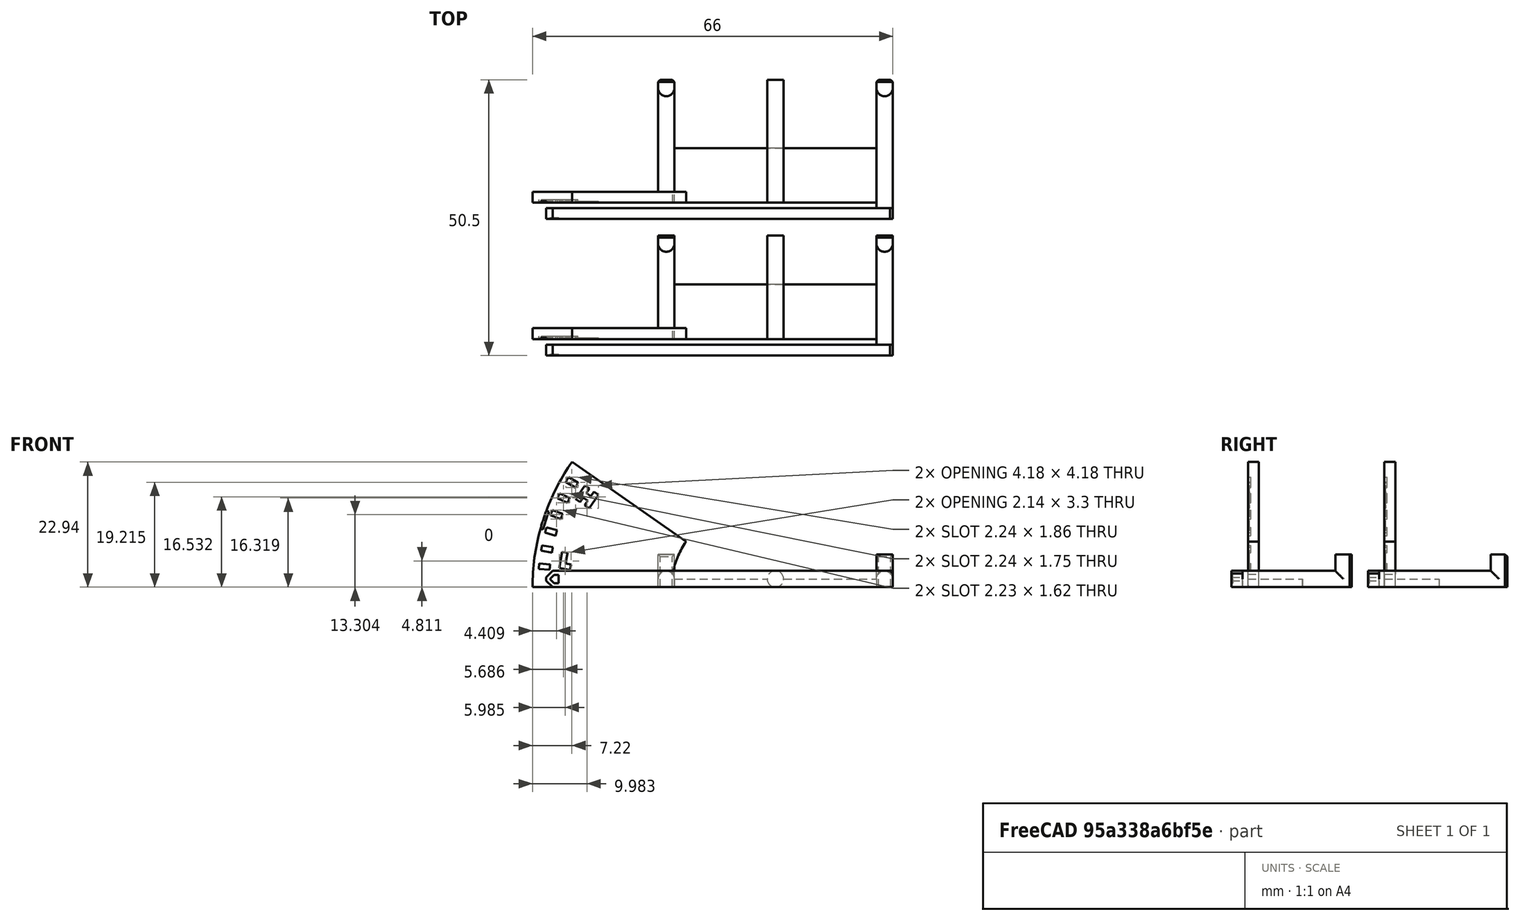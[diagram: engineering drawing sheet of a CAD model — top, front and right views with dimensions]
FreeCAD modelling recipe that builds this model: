
FCSTD DOCUMENT  (FreeCAD 0.18R16146 (Git))
Label: belt-tension-meter-lite
License: All rights reserved
LicenseURL: http://en.wikipedia.org/wiki/All_rights_reserved
objects: Part::Box×20, Part::Cylinder×11, Part::Cut×8, Part::MultiFuse×6, Part::Chamfer×4, Part::Feature×4, Part::MultiCommon×2, Mesh::Feature×1
note: 55 computed .brp shape members not serialized (recipe doc carries the construction recipe); baked Part::Feature solids carry a one-line shape summary decoded from their .brp

FEATURE [Mesh::Feature] belt
  Placement = pos=(-127.5,-93.9,0) rot=(0,0,1;0rad)
FEATURE [Part::Cylinder] Cylinder
  Angle = 35
  AttacherType = Attacher::AttachEngine3D
  Height = 2
  Placement = pos=(17,3,-1e-15) rot=(0,0.707107,0.707107;3.14159rad)
  Radius = 40
FEATURE [Part::Cylinder] Cylinder001
  Angle = 360
  AttacherType = Attacher::AttachEngine3D
  Height = 2
  Placement = pos=(17,3,-1e-15) rot=(-1,0,0;1.5708rad)
  Radius = 14.5
FEATURE [Part::Box] Box  label="Cube"
  AttacherType = Attacher::AttachEngine3D
  Height = 3
  Length = 63.5
  Placement = pos=(-20.5,0,0) rot=(0,0,1;0rad)
  Width = 2
FEATURE [Part::Cylinder] Cylinder002
  Angle = 360
  AttacherType = Attacher::AttachEngine3D
  Height = 19
  Placement = pos=(1.5,3,1.5) rot=(-1,0,0;1.5708rad)
  Radius = 1.5
FEATURE [Part::Cylinder] Cylinder003
  Angle = 360
  AttacherType = Attacher::AttachEngine3D
  Height = 4.5
  Placement = pos=(1.5,20.5,1.5) rot=(0,0,1;0rad)
  Radius = 1.5
FEATURE [Part::Cylinder] Cylinder004
  Angle = 360
  AttacherType = Attacher::AttachEngine3D
  Height = 19
  Placement = pos=(21.5,3,1.5) rot=(-1,0,0;1.5708rad)
  Radius = 1.5
FEATURE [Part::Cylinder] Cylinder005
  Angle = 360
  AttacherType = Attacher::AttachEngine3D
  Height = 22
  Placement = pos=(41.5,0,1.5) rot=(-1,0,0;1.5708rad)
  Radius = 1.5
FEATURE [Part::Cylinder] Cylinder006
  Angle = 360
  AttacherType = Attacher::AttachEngine3D
  Height = 4.5
  Placement = pos=(41.5,20.5,1.5) rot=(0,0,1;0rad)
  Radius = 1.5
FEATURE [Part::Box] Box001  label="Cube001"
  AttacherType = Attacher::AttachEngine3D
  Height = 1.5
  Length = 43
  Placement = pos=(0,3,0) rot=(0,0,1;0rad)
  Width = 10
FEATURE [Part::Box] Box002  label="Cube002"
  AttacherType = Attacher::AttachEngine3D
  Height = 1.5
  Length = 3
  Placement = pos=(40,2,0) rot=(0,0,1;0rad)
  Width = 20
FEATURE [Part::Box] Box003  label="Cube003"
  AttacherType = Attacher::AttachEngine3D
  Height = 1.5
  Length = 3
  Placement = pos=(0,3,0) rot=(0,0,1;0rad)
  Width = 19
FEATURE [Part::Box] Box004  label="Cube004"
  AttacherType = Attacher::AttachEngine3D
  Height = 6
  Length = 3
  Placement = pos=(0,20.5,0) rot=(0,0,1;0rad)
  Width = 1.5
FEATURE [Part::Box] Box005  label="Cube005"
  AttacherType = Attacher::AttachEngine3D
  Height = 6
  Length = 3
  Placement = pos=(40,20.5,0) rot=(0,0,1;0rad)
  Width = 1.5
FEATURE [Part::Cylinder] Cylinder007
  Angle = 360
  AttacherType = Attacher::AttachEngine3D
  Height = 15
  Placement = pos=(17,3,-1e-15) rot=(-1,0,0;1.5708rad)
  Radius = 37
FEATURE [Part::Box] Box007  label="Cube007"
  AttacherType = Attacher::AttachEngine3D
  Height = 63
  Length = 1
  Placement = pos=(16.5,3,0) rot=(0,-1,0;1.48353rad)
  Width = 0.5
FEATURE [Part::Box] Box008  label="Cube008"
  AttacherType = Attacher::AttachEngine3D
  Height = 63
  Length = 1
  Placement = pos=(16.5,3,0) rot=(0,-1,0;1.39626rad)
  Width = 0.5
FEATURE [Part::Box] Box009  label="Cube009"
  AttacherType = Attacher::AttachEngine3D
  Height = 63
  Length = 1
  Placement = pos=(16.5,3,0) rot=(0,-1,0;1.309rad)
  Width = 0.5
FEATURE [Part::Box] Box010  label="Cube010"
  AttacherType = Attacher::AttachEngine3D
  Height = 63
  Length = 1
  Placement = pos=(16.5,3,0) rot=(0,-1,0;1.22173rad)
  Width = 0.5
FEATURE [Part::Box] Box011  label="Cube011"
  AttacherType = Attacher::AttachEngine3D
  Height = 63
  Length = 1
  Placement = pos=(16.5,3,0) rot=(0,-1,0;1.13446rad)
  Width = 0.5
FEATURE [Part::Box] Box012  label="Cube012"
  AttacherType = Attacher::AttachEngine3D
  Height = 63
  Length = 1
  Placement = pos=(16.5,3,0) rot=(0,-1,0;1.0472rad)
  Width = 0.5
FEATURE [Part::MultiFuse] Fusion
  Shapes = -> [Box012,Box011,Box010,Box009,Box008,Box007]
FEATURE [Part::Cut] Cut
  Base = -> Cylinder
  Tool = -> Cylinder001
FEATURE [Part::Cylinder] Cylinder008
  Angle = 360
  AttacherType = Attacher::AttachEngine3D
  Height = 15
  Placement = pos=(17,3,-1e-15) rot=(-1,0,0;1.5708rad)
  Radius = 39
FEATURE [Part::MultiCommon] Common
  Shapes = -> [Fusion,Cylinder008]
FEATURE [Part::Cut] Cut001
  Base = -> Common
  Tool = -> Cylinder007
FEATURE [Part::Cut] Cut002
  Base = -> Cut
  Tool = -> Cut001
FEATURE [Part::Chamfer] Chamfer
  Base = -> Box
  Edges = 2 edges r=1.2: [Edge2,Edge4]
FEATURE [Part::MultiFuse] Fusion001
  Shapes = -> [Chamfer,Box001,Box002,Cut002,Cylinder003,Box003,Cylinder004,Box004,Cylinder005,Box005,Cylinder006,Cylinder002]
FEATURE [Part::Box] Box013  label="Cube013"
  AttacherType = Attacher::AttachEngine3D
  Height = 3
  Length = 1
  Width = 1
FEATURE [Part::Box] Box014  label="Cube014"
  AttacherType = Attacher::AttachEngine3D
  Height = 3
  Length = 1
  Placement = pos=(2,0,0) rot=(0,0,1;0rad)
  Width = 1
FEATURE [Part::Box] Box015  label="Cube015"
  AttacherType = Attacher::AttachEngine3D
  Height = 1
  Length = 1
  Placement = pos=(1,0,1) rot=(0,0,1;0rad)
  Width = 1
FEATURE [Part::MultiFuse] Fusion002
  Placement = pos=(-15.1059,0,16.164) rot=(0,1,0;0.610865rad)
  Shapes = -> [Box015,Box014,Box013]
FEATURE [Part::Box] Box016  label="Cube016"
  AttacherType = Attacher::AttachEngine3D
  Height = 3
  Length = 1
  Width = 1
FEATURE [Part::Box] Box017  label="Cube017"
  AttacherType = Attacher::AttachEngine3D
  Height = 1
  Length = 1
  Placement = pos=(1,0,0) rot=(0,0,1;0rad)
  Width = 1
FEATURE [Part::MultiFuse] Fusion003
  Placement = pos=(-18.0868,0,3.5076) rot=(0,1,0;0.174533rad)
  Shapes = -> [Box017,Box016]
FEATURE [Part::MultiFuse] Fusion004
  Placement = pos=(0,2.25,0) rot=(0,0,1;0rad)
  Shapes = -> [Fusion002,Fusion003]
FEATURE [Part::Cut] Cut003
  Base = -> Fusion001
  Tool = -> Fusion004
FEATURE [Part::Cylinder] Cylinder009
  Angle = 5
  AttacherType = Attacher::AttachEngine3D
  Height = 15
  Placement = pos=(17,3,-1e-15) rot=(0.09579,0.703855,0.703855;3.33259rad)
  Radius = 39.5
FEATURE [Part::Cylinder] Cylinder010
  Angle = 5
  AttacherType = Attacher::AttachEngine3D
  Height = 15
  Placement = pos=(17,3,-1e-15) rot=(0.09579,0.703855,0.703855;3.33259rad)
  Radius = 40
FEATURE [Part::Cut] Cut004
  Base = -> Cylinder010
  Placement = pos=(0,-14.75,0) rot=(0,0,1;0rad)
  Tool = -> Cylinder009
FEATURE [Part::Cut] Cut005
  Base = -> Cut003
  Tool = -> Cut004
FEATURE [Part::Box] Box018  label="Cube018"
  AttacherType = Attacher::AttachEngine3D
  Height = 1.5
  Length = 1.5
  Placement = pos=(-19.75,-1,0.75) rot=(0,0,1;0rad)
  Width = 1
FEATURE [Part::Chamfer] Chamfer001
  Base = -> Box018
  Edges = 2 edges r=0.7: [Edge2,Edge4]
  Placement = pos=(0,0.25,0) rot=(0,0,1;0rad)
FEATURE [Part::Cut] Cut006
  Base = -> Cut005
  Tool = -> Chamfer001
FEATURE [Part::Feature] Cut006001  label="Cut007"
  shape: bbox 66 x 22 x 22.94 mm, 93 faces (baked)
FEATURE [Part::Chamfer] Chamfer002
  Base = -> Cut006001
  Edges = 1 edges r=0.5: [Edge221]
FEATURE [Part::Chamfer] Chamfer003
  Base = -> Chamfer002
  Edges = 6 edges r=0.4: [Edge11,Edge47,Edge49,Edge137,Edge138,Edge139]
FEATURE [Part::Feature] Chamfer003001  label="Chamfer004"
  Placement = pos=(0,25,0) rot=(0,0,1;0rad)
  shape: bbox 66 x 22 x 22.94 mm, 100 faces (baked)
FEATURE [Part::Box] Box019  label="Cube019"
  AttacherType = Attacher::AttachEngine3D
  Height = 10
  Length = 45
  Placement = pos=(0,38,0) rot=(0,0,1;0rad)
  Width = 10
FEATURE [Part::Feature] Chamfer003002  label="Chamfer005"
  Placement = pos=(0,25,0) rot=(0,0,1;0rad)
  shape: bbox 66 x 22 x 22.94 mm, 100 faces (baked)
FEATURE [Part::Box] Box020  label="Cube020"
  AttacherType = Attacher::AttachEngine3D
  Height = 10
  Length = 45
  Placement = pos=(0,43,0) rot=(0,0,1;0rad)
  Width = 10
FEATURE [Part::MultiCommon] Common001
  Placement = pos=(0,3.5,0) rot=(0,0,1;0rad)
  Shapes = -> [Box019,Chamfer003001]
FEATURE [Part::Cut] Cut006002
  Base = -> Chamfer003002
  Tool = -> Box020
FEATURE [Part::MultiFuse] Fusion005
  Shapes = -> [Common001,Cut006002]
FEATURE [Part::Feature] Fusion005001  label="Fusion006"
  shape: bbox 66 x 25.5 x 22.94 mm, 100 faces (baked)
